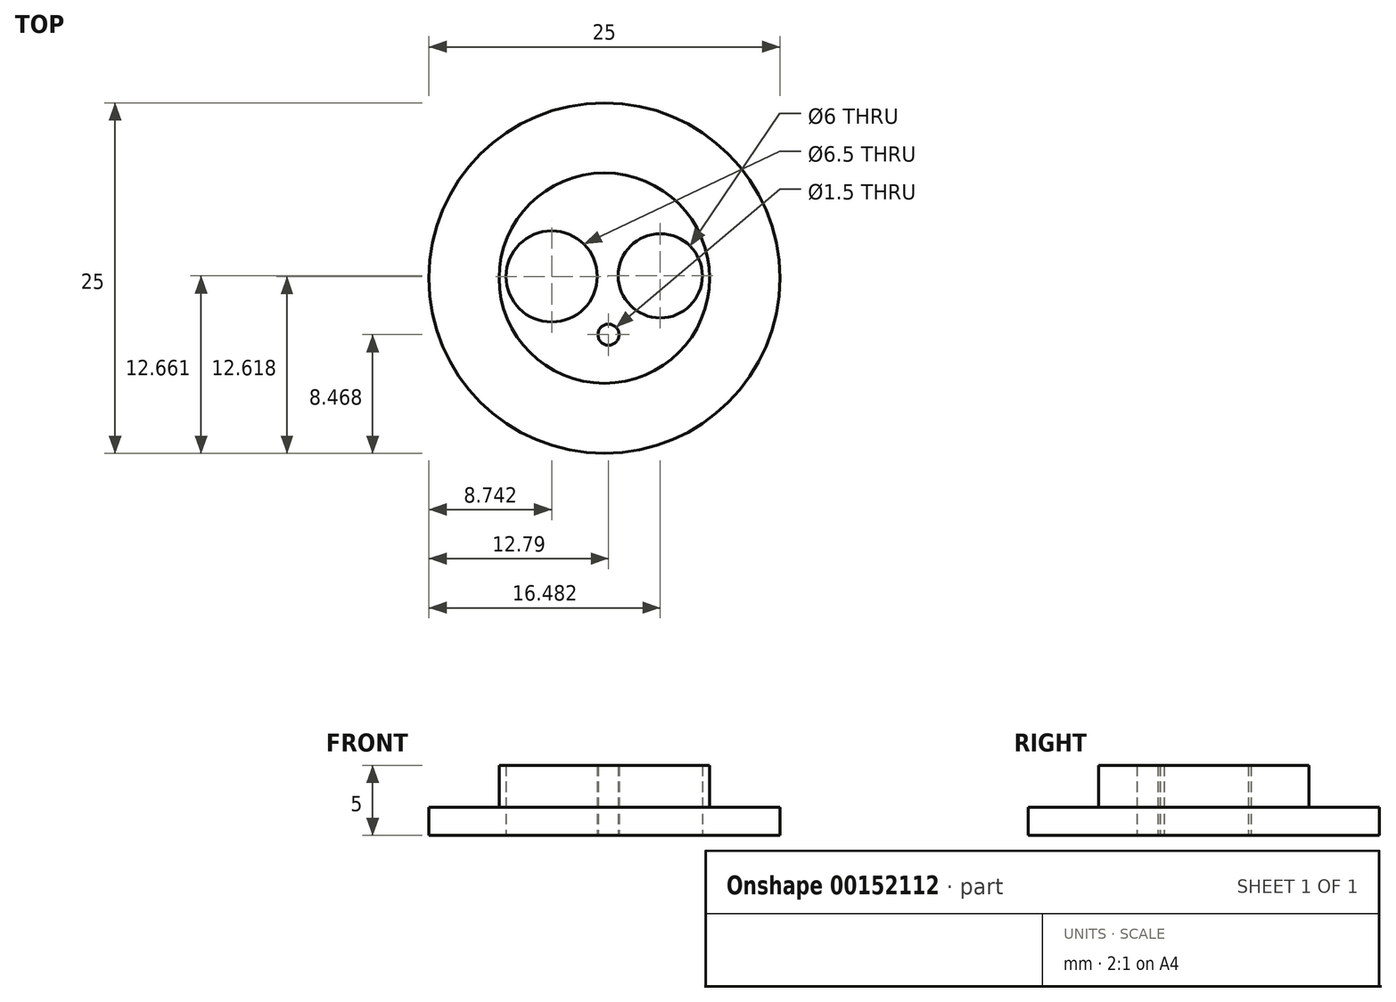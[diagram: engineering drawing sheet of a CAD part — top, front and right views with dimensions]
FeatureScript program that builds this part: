
annotation { "Feature Type Name" : "Feature", "Feature Type Description" : "" }
export const myFeature = defineFeature(function(context is Context, id is Id, definition is map)
    precondition{}
    {
        {
            var Q0;
            Q0=qCreatedBy(makeId("Top.planeOp"),FACE);
            var sketch = newSketch(context, id + "F0", { "sketchPlane" : qUnion([Q0])});
            skCircle(sketch, "E0", {"center": v(-10.09, -27.18) * mm, "radius": 3.25 * mm});
            skCircle(sketch, "E1", {"center": v(-2.35, -27.14) * mm, "radius": 3 * mm});
            skCircle(sketch, "E2", {"center": v(-6.04, -31.33) * mm, "radius": 0.75 * mm});
            skCircle(sketch, "E3", {"center": v(-6.33, -27.3) * mm, "radius": 8 * mm});
            skCircle(sketch, "E4", {"center": v(-6.33, -27.3) * mm, "radius": 12.5 * mm});
            skSolve(sketch);
        }
        {
            var Q0;
            Q0 = qSketchRegion(id + "F0", true);
            var Q1;
            Q1=makeQuery(id+"F0.imprint","IMPRINT",FACE,{"disambiguationData":[TD([[makeQuery(id+"F0.imprint","IMPRINT",EDGE,{"derivedFrom":sQuery(id+"F0.wireOp",EDGE,"E0")}),-1.0]])]});
            extrude(context, id + "F1", {"entities" : qUnion([Q0, Q1]), "depth" : 5 * mm});
        }
        {
            var Q0;
            Q0=makeQuery(id+"F1.opExtrude","CAP_FACE",FACE,{"disambiguationData":[OSD([sQuery(id+"F0.wireOp",EDGE,"E0"),sQuery(id+"F0.wireOp",EDGE,"E1"),sQuery(id+"F0.wireOp",EDGE,"E2"),sQuery(id+"F0.wireOp",EDGE,"E4")])],"isStart":false});
            var sketch = newSketch(context, id + "F2", { "sketchPlane" : qUnion([Q0])});
            skCircle(sketch, "E5", {"center": v(-6.33, -27.3) * mm, "radius": 7.5 * mm});
            skSolve(sketch);
        }
        {
            var Q0;
            Q0=makeQuery(id+"F2.imprint","IMPRINT",FACE,{"disambiguationData":[TD([[makeQuery(id+"F2.imprint","IMPRINT",EDGE,{"derivedFrom":sQuery(id+"F2.wireOp",EDGE,"E5")}),-1.0]])]});
            extrude(context, id + "F3", {"entities" : qUnion([Q0]), "operationType" : NewBodyOperationType.REMOVE, "oppositeDirection" : true, "depth" : 3 * mm});
        }
    });
